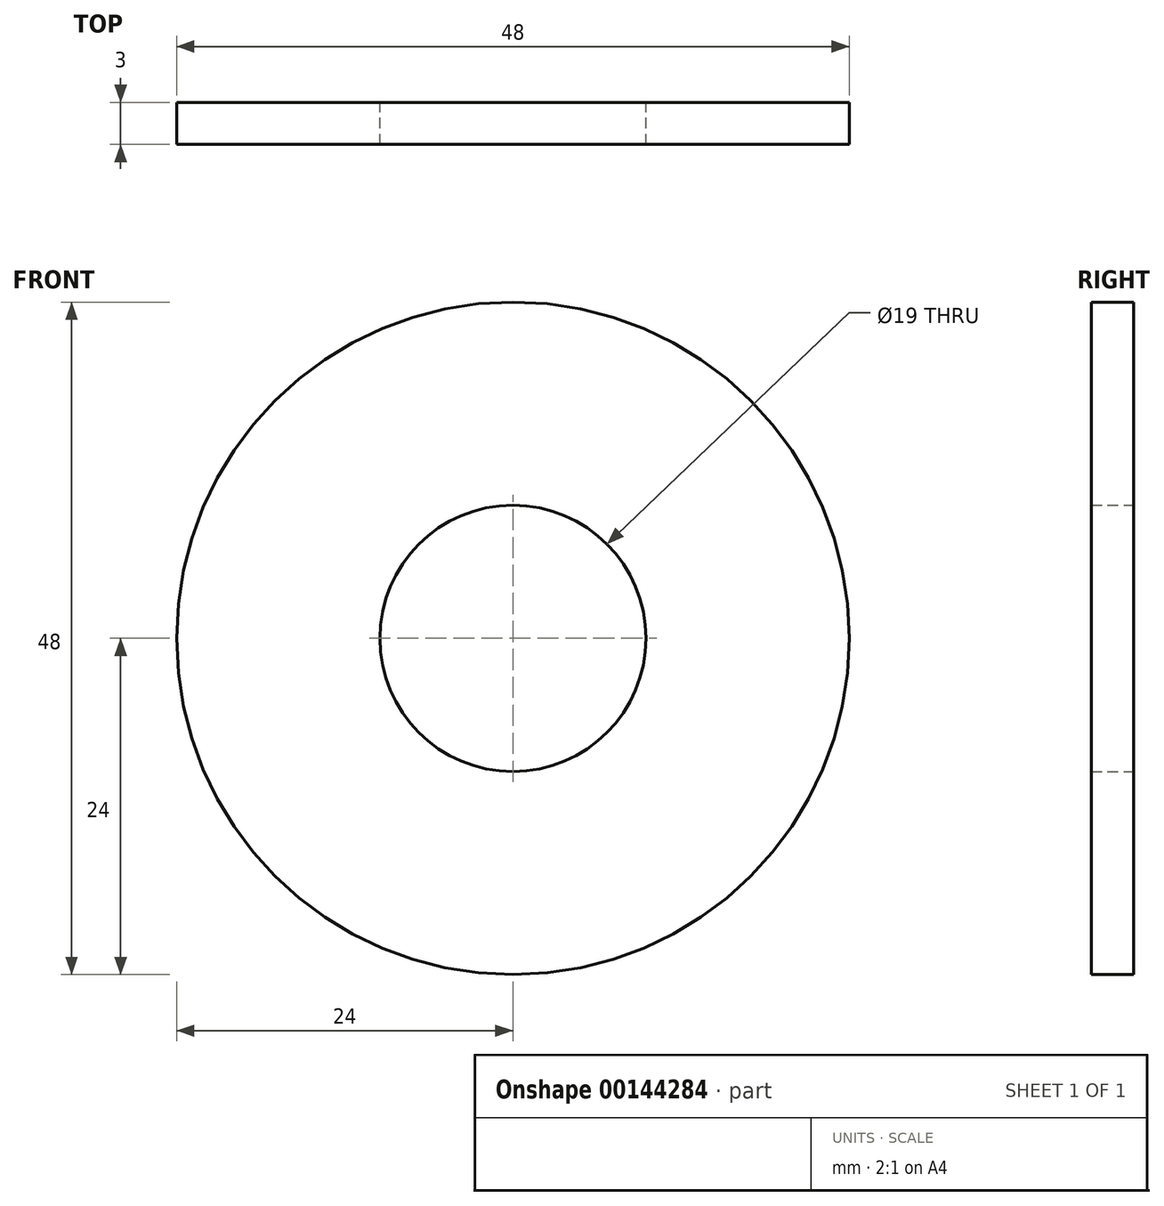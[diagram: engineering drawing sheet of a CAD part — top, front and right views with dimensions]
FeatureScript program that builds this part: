
annotation { "Feature Type Name" : "Feature", "Feature Type Description" : "" }
export const myFeature = defineFeature(function(context is Context, id is Id, definition is map)
    precondition{}
    {
        {
            var Q0;
            Q0=qCreatedBy(makeId("Front.planeOp"),FACE);
            var sketch = newSketch(context, id + "F0", { "sketchPlane" : qUnion([Q0])});
            skCircle(sketch, "E0", {"center": v(0, 0) * mm, "radius": 24 * mm});
            skCircle(sketch, "E1", {"center": v(0, 0) * mm, "radius": 9.5 * mm});
            skSolve(sketch);
        }
        {
            var Q0;
            Q0=makeQuery(id+"F0.imprint","IMPRINT",FACE,{"disambiguationData":[TD([[makeQuery(id+"F0.imprint","IMPRINT",EDGE,{"derivedFrom":sQuery(id+"F0.wireOp",EDGE,"E0")}),1.0]])]});
            extrude(context, id + "F1", {"entities" : qUnion([Q0]), "endBound" : BoundingType.SYMMETRIC, "depth" : 3 * mm});
        }
    });
